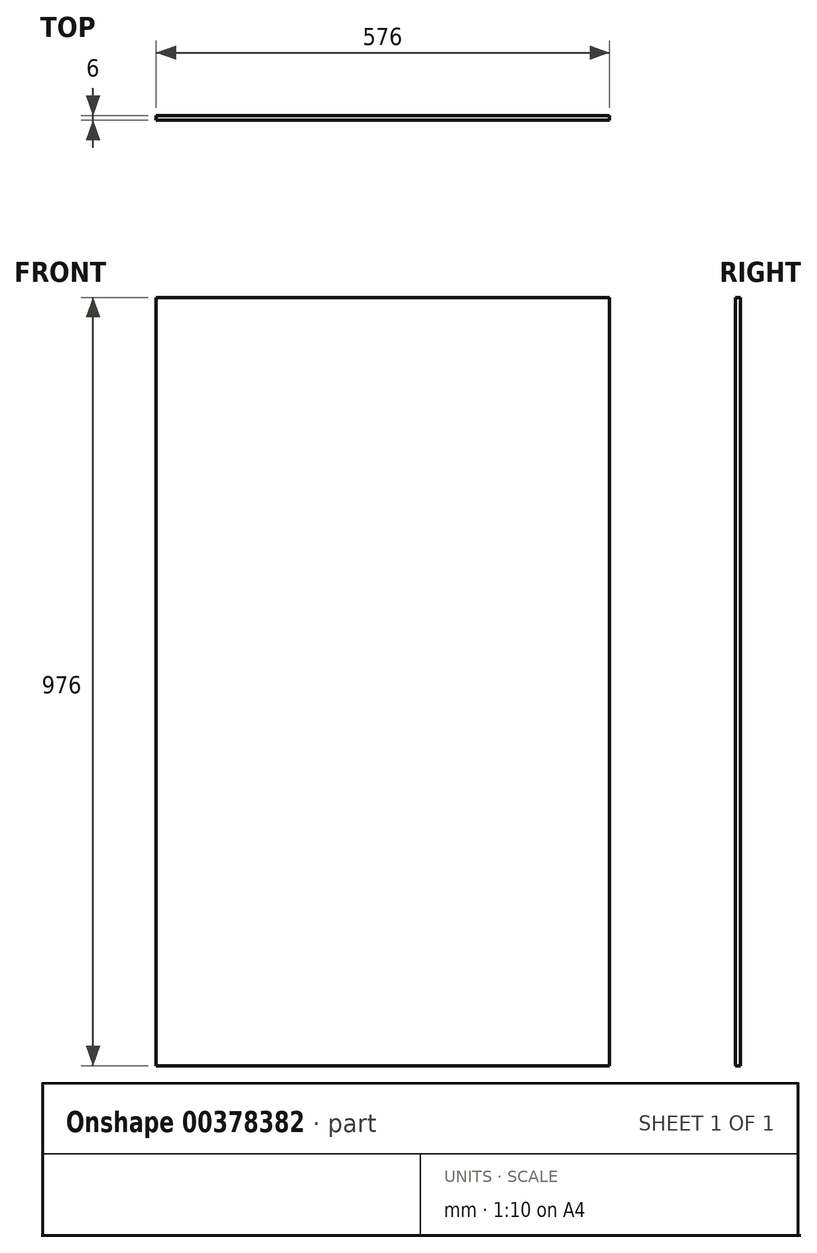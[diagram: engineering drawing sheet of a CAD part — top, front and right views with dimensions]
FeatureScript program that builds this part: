
annotation { "Feature Type Name" : "Feature", "Feature Type Description" : "" }
export const myFeature = defineFeature(function(context is Context, id is Id, definition is map)
    precondition{}
    {
        {
            var Q0;
            Q0=qCreatedBy(makeId("Front.planeOp"),FACE);
            var sketch = newSketch(context, id + "F0", { "sketchPlane" : qUnion([Q0])});
            skLineSegment(sketch, "E0.bottom", {"start": v(288, 488) * mm, "end": v(-288, 488) * mm});
            skLineSegment(sketch, "E0.top", {"start": v(288, -488) * mm, "end": v(-288, -488) * mm});
            skLineSegment(sketch, "E0.left", {"start": v(288, 488) * mm, "end": v(288, -488) * mm});
            skLineSegment(sketch, "E0.right", {"start": v(-288, 488) * mm, "end": v(-288, -488) * mm});
            skPoint(sketch, "E0.middle", {"position": v(0, 0) * mm});
            skSolve(sketch);
        }
        {
            var Q0;
            Q0=qSketchRegion(id+"F0",true);
            extrude(context, id + "F1", {"entities" : qUnion([Q0]), "depth" : 6 * mm});
        }
    });
